# Revit family: UNB_Specchio_Multiproduct_BIM_IT_T3345;T3346;T3347;T3348;T3349_NEW
name_source: partatom
category: Plumbing Fixtures
revit_build: Autodesk Revit 2017 (Build: 20160225_1515(x64)
units: mm (PartAtom-declared; Revit-internal decimal feet)

## family parameters
Cut with Voids When Loaded = No
Host = Face
Part Type = Normal
Room Calculation Point = No
Round Connector Dimension = Use Diameter
Shared = No

## types (5) — shared parameters
Accessori = http://www.idealstandard.it
AltezzaNominale = 700 mm  [stored 2.29659 ft]
Autore = Ideal Standard
Brand = Ideal Standard
CodiceDiPrestazione = EN
Colore = specchio
Connessione = piombatura
Default Elevation = 1500 mm  [stored 4.92126 ft]
DescrizioneClassifcazioneUni2015 = Bathroom furniture
Finitura = specchio
Forma = rettangolare
Garanzia = garanzia del produttore
IfcEsportaCome = BATHROOM FURNITURE
InformazioniDiProdotto = http://www.idealstandard.it
InstruzioniInstallazione = http://www.idealstandard.it
LunghezzaNominale = 26 mm
Materiale = bicchiere
PartiDiRicambio = http://www.idealstandard.it
ProfonditàNominale = 26 mm
Revisione = 1
RiferimentoClassificazioneUni2015 = MIRRORS
Spazio = interno
Telefono = 800 652 290
TipoDiDato = Fisso
TipoEspotazioneIfc = IfcFurnitureType
TipologiaVaso = Altro
URL = http://www.idealstandard.it
UnitàDurata = anno
UnitàDurataGaranzia = anno
UnitàLineare = millimetro
UnitàMonetaria = €
UnitàSuperficie = millimetro
UnitàVolume = litro
Versione = 1
VersioneClassificazioneUni2015 = IfcFurnitureType
zero-valued in all types: Cost, CostoDiSostituzione

## per-type parameters (varying)
| type | Caratteristiche | CodiceABarre | Description | LarghezzaNominale | Model | ModelloDiRiferimento | Nome | NomeOggettoBim | NumeroDiModello | PesoNetto | Riferimento |
| T3345 - 500 x 700 mirror | SPECCHIO HIGH LIGHT 50X70 38,6W 230W | 8014140447375 | SPECCHIO HIGH LIGHT 50X70 38,6W 230W | 500 mm  [stored 1.64042 ft] | T3345BH | SPECCHIO HIGH LIGHT 50X70 38,6W 230W | ISI_IdealStandard_Specchio_T3345 | ISI_IdealStandard_Specchio_T3345 | T3345BH | 4.95 Kg | T3345 |
| T3346 - 600 x 700 mirror | SPECCHIO HIGH LIGHT 60X70 40,5W 230W | 8014140447382 | SPECCHIO HIGH LIGHT 60X70 40,5W 230W | 600 mm | T3346BH | SPECCHIO HIGH LIGHT 60X70 40,5W 230W | ISI_IdealStandard_Specchio_T3346 | ISI_IdealStandard_Specchio_T3346 | T3346BH | 5.67 Kg | T3346 |
| T3347 - 800 x 700 mirror | SPECCHIO HIGH LIGHT 80X70 44,3W 230W | 8014140447399 | SPECCHIO HIGH LIGHT 80X70 44,3W 230W | 800 mm  [stored 2.62467 ft] | T3347BH | SPECCHIO HIGH LIGHT 80X70 44,3W 230W | ISI_IdealStandard_Specchio_T3347 | ISI_IdealStandard_Specchio_T3347 | T3347BH | 7.02 Kg | T3347 |
| T3348 - 1000 x 700 mirror | SPECCHIO HIGH LIGHT 100X70 76,1W 230W | 8014140447405 | SPECCHIO HIGH LIGHT 100X70 76,1W 230W | 1000 mm  [stored 3.28084 ft] | T3348BH | SPECCHIO HIGH LIGHT 100X70 76,1W 230W | ISI_IdealStandard_Specchio_T3348 | ISI_IdealStandard_Specchio_T3348 | T3348BH | 8.64 Kg | T3348 |
| T3349 - 1200 x 700 mirror | SPECCHIO HIGH LIGHT 120X70 80W 230W | 8014140447412 | SPECCHIO HIGH LIGHT 120X70 80W 230W | 1200 mm  [stored 3.93701 ft] | T3349BH | SPECCHIO HIGH LIGHT 120X70 80W 230W | ISI_IdealStandard_Specchio_T3349 | ISI_IdealStandard_Specchio_T3349 | T3349BH | 10.04 Kg | T3349 |

note: [stored X ft] marks values corroborated as IEEE doubles in the binary element streams (Revit-internal decimal feet)

## geometry (parser evidence)
native form markers: Sweep x1
no freeform markers — native parametric forms only
